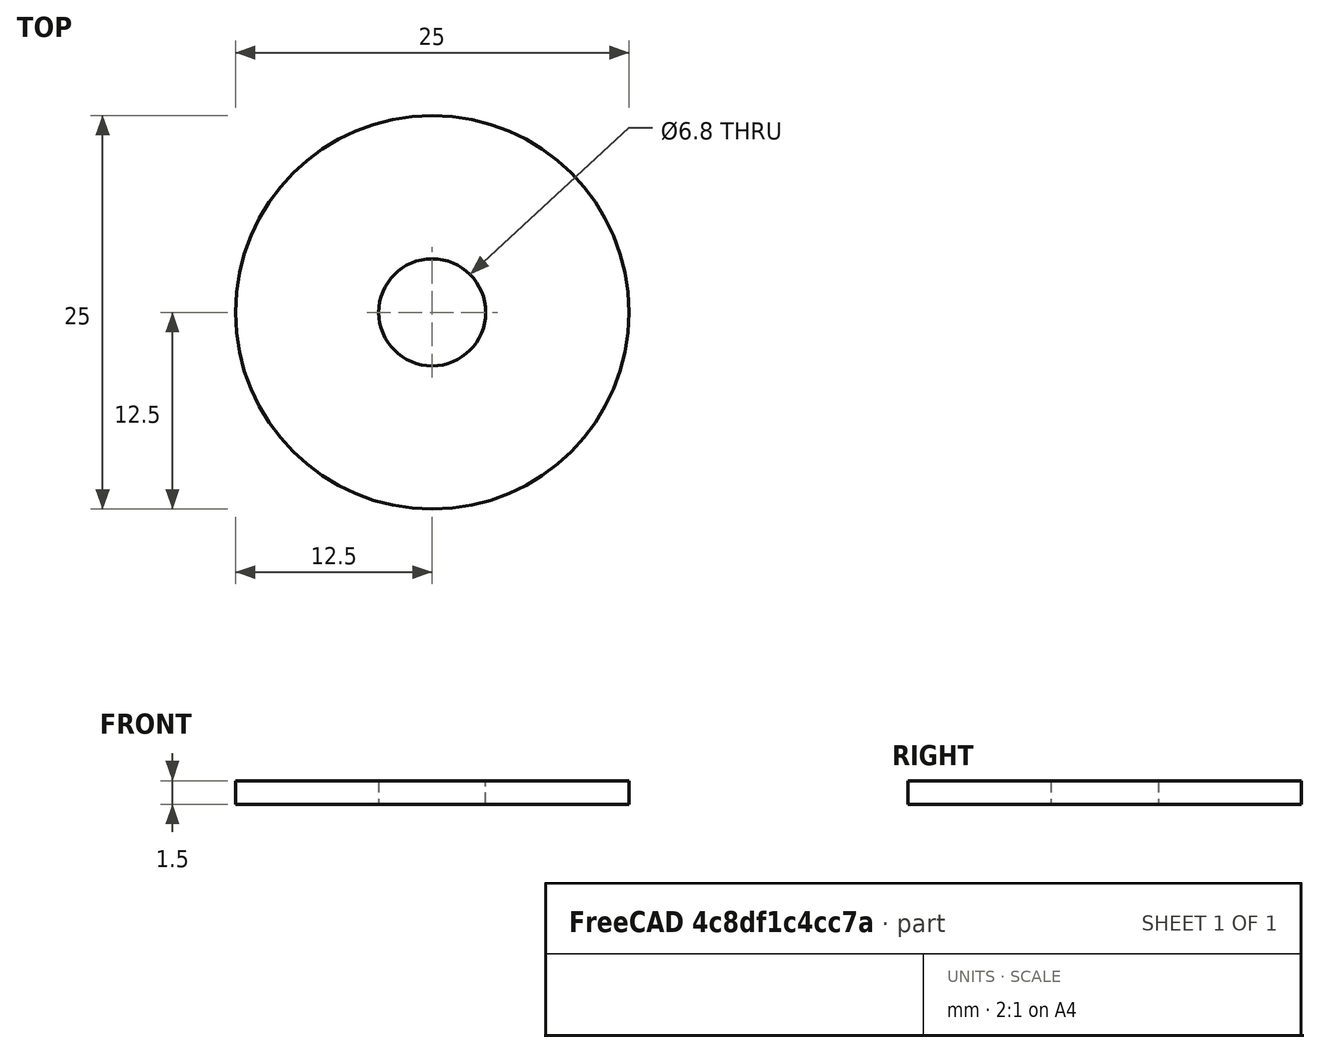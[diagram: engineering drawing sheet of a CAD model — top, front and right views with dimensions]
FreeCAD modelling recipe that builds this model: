
FCSTD DOCUMENT  (FreeCAD 0.21R33694 (Git))
Label: volume knob mount
License: All rights reserved
LicenseURL: http://en.wikipedia.org/wiki/All_rights_reserved
objects: Sketcher::SketchObject×1, PartDesign::Pad×1, PartDesign::Body×1
note: 4 computed .brp shape members not serialized (recipe doc carries the construction recipe); baked Part::Feature solids carry a one-line shape summary decoded from their .brp

FEATURE [Sketcher::SketchObject] Sketch
  FullyConstrained = true
  MapMode = 5
  Support = -> [XY_Plane]
  sketch-geometry (2):
    g0: Circle CenterX=0 CenterY=0 CenterZ=0 NormalX=0 NormalY=0 NormalZ=1 AngleXU=0 Radius=12.5
    g1: Circle CenterX=0 CenterY=0 CenterZ=0 NormalX=0 NormalY=0 NormalZ=1 AngleXU=0 Radius=3.4
  constraints (4):
    c: Coincident(g1,g0)
    c: Coincident(g0,g-1)
    c: Diameter(g0) = 25
    c: Diameter(g1) = 6.8
FEATURE [PartDesign::Pad] Pad
  Direction = (0,0,1)
  Length = 1.5
  Length2 = 10
  Profile = -> Sketch
  ReferenceAxis = -> Sketch [N_Axis]
  Refine = true
  Type = 0
FEATURE [PartDesign::Body] Body
  Group = -> [Sketch,Pad]
  Origin = -> Origin
  Tip = -> Pad
